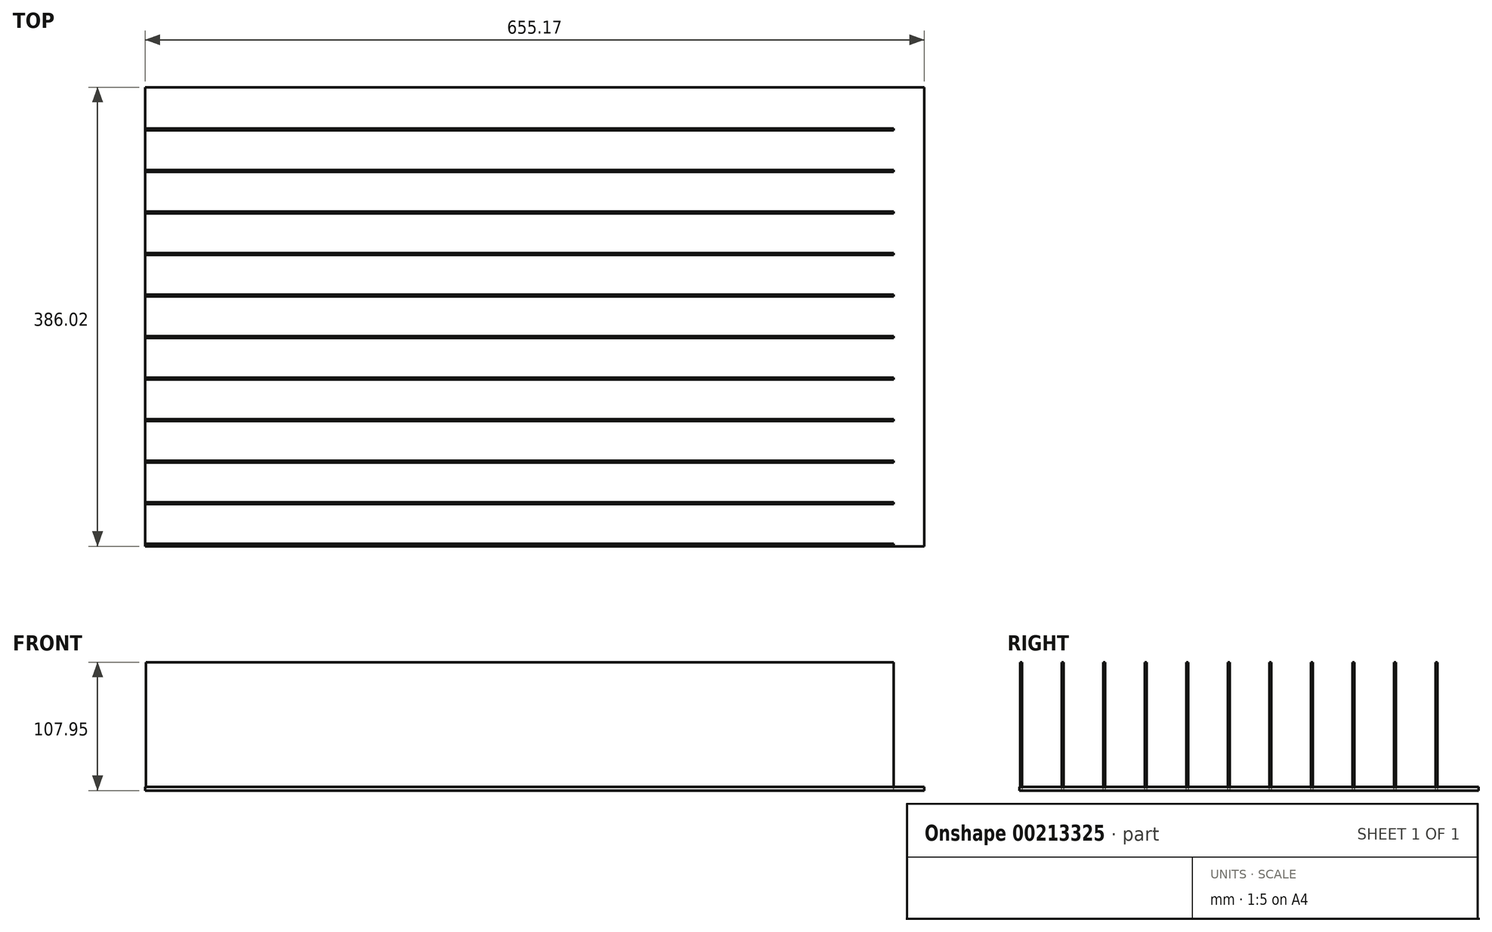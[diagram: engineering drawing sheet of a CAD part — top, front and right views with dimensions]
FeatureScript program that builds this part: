
annotation { "Feature Type Name" : "Feature", "Feature Type Description" : "" }
export const myFeature = defineFeature(function(context is Context, id is Id, definition is map)
    precondition{}
    {
        {
            var Q0;
            Q0=qCreatedBy(makeId("Right.planeOp"),FACE);
            var sketch = newSketch(context, id + "F0", { "sketchPlane" : qUnion([Q0])});
            skLineSegment(sketch, "E0", {"start": v(-1.59, 0) * mm, "end": v(-1.59, 107.95) * mm});
            skLineSegment(sketch, "E1", {"start": v(-1.59, 107.95) * mm, "end": v(0, 107.95) * mm});
            skLineSegment(sketch, "E2", {"start": v(0, 107.95) * mm, "end": v(0, 0) * mm});
            skLineSegment(sketch, "E3", {"start": v(0, 0) * mm, "end": v(-1.59, 0) * mm});
            skLineSegment(sketch, "E4.1.0.0", {"start": v(34.93, 107.95) * mm, "end": v(34.93, 0) * mm});
            skLineSegment(sketch, "E4.1.0.1", {"start": v(33.34, 0) * mm, "end": v(33.34, 107.95) * mm});
            skLineSegment(sketch, "E4.1.0.2", {"start": v(33.34, 107.95) * mm, "end": v(34.93, 107.95) * mm});
            skLineSegment(sketch, "E4.1.0.3", {"start": v(34.93, 0) * mm, "end": v(33.34, 0) * mm});
            skLineSegment(sketch, "E4.2.0.0", {"start": v(69.85, 107.95) * mm, "end": v(69.85, 0) * mm});
            skLineSegment(sketch, "E4.2.0.1", {"start": v(68.26, 0) * mm, "end": v(68.26, 107.95) * mm});
            skLineSegment(sketch, "E4.2.0.2", {"start": v(68.26, 107.95) * mm, "end": v(69.85, 107.95) * mm});
            skLineSegment(sketch, "E4.2.0.3", {"start": v(69.85, 0) * mm, "end": v(68.26, 0) * mm});
            skLineSegment(sketch, "E4.3.0.0", {"start": v(104.78, 107.95) * mm, "end": v(104.78, 0) * mm});
            skLineSegment(sketch, "E4.3.0.1", {"start": v(103.19, 0) * mm, "end": v(103.19, 107.95) * mm});
            skLineSegment(sketch, "E4.3.0.2", {"start": v(103.19, 107.95) * mm, "end": v(104.78, 107.95) * mm});
            skLineSegment(sketch, "E4.3.0.3", {"start": v(104.78, 0) * mm, "end": v(103.19, 0) * mm});
            skLineSegment(sketch, "E4.4.0.0", {"start": v(139.7, 107.95) * mm, "end": v(139.7, 0) * mm});
            skLineSegment(sketch, "E4.4.0.1", {"start": v(138.11, 0) * mm, "end": v(138.11, 107.95) * mm});
            skLineSegment(sketch, "E4.4.0.2", {"start": v(138.11, 107.95) * mm, "end": v(139.7, 107.95) * mm});
            skLineSegment(sketch, "E4.4.0.3", {"start": v(139.7, 0) * mm, "end": v(138.11, 0) * mm});
            skLineSegment(sketch, "E4.5.0.0", {"start": v(174.63, 107.95) * mm, "end": v(174.63, 0) * mm});
            skLineSegment(sketch, "E4.5.0.1", {"start": v(173.04, 0) * mm, "end": v(173.04, 107.95) * mm});
            skLineSegment(sketch, "E4.5.0.2", {"start": v(173.04, 107.95) * mm, "end": v(174.62, 107.95) * mm});
            skLineSegment(sketch, "E4.5.0.3", {"start": v(174.62, 0) * mm, "end": v(173.04, 0) * mm});
            skLineSegment(sketch, "E4.6.0.0", {"start": v(209.55, 107.95) * mm, "end": v(209.55, 0) * mm});
            skLineSegment(sketch, "E4.6.0.1", {"start": v(207.96, 0) * mm, "end": v(207.96, 107.95) * mm});
            skLineSegment(sketch, "E4.6.0.2", {"start": v(207.96, 107.95) * mm, "end": v(209.55, 107.95) * mm});
            skLineSegment(sketch, "E4.6.0.3", {"start": v(209.55, 0) * mm, "end": v(207.96, 0) * mm});
            skLineSegment(sketch, "E4.7.0.0", {"start": v(244.48, 107.95) * mm, "end": v(244.48, 0) * mm});
            skLineSegment(sketch, "E4.7.0.1", {"start": v(242.89, 0) * mm, "end": v(242.89, 107.95) * mm});
            skLineSegment(sketch, "E4.7.0.2", {"start": v(242.89, 107.95) * mm, "end": v(244.48, 107.95) * mm});
            skLineSegment(sketch, "E4.7.0.3", {"start": v(244.48, 0) * mm, "end": v(242.89, 0) * mm});
            skLineSegment(sketch, "E4.8.0.0", {"start": v(279.4, 107.95) * mm, "end": v(279.4, 0) * mm});
            skLineSegment(sketch, "E4.8.0.1", {"start": v(277.81, 0) * mm, "end": v(277.81, 107.95) * mm});
            skLineSegment(sketch, "E4.8.0.2", {"start": v(277.81, 107.95) * mm, "end": v(279.4, 107.95) * mm});
            skLineSegment(sketch, "E4.8.0.3", {"start": v(279.4, 0) * mm, "end": v(277.81, 0) * mm});
            skLineSegment(sketch, "E4.9.0.0", {"start": v(314.33, 107.95) * mm, "end": v(314.33, 0) * mm});
            skLineSegment(sketch, "E4.9.0.1", {"start": v(312.74, 0) * mm, "end": v(312.74, 107.95) * mm});
            skLineSegment(sketch, "E4.9.0.2", {"start": v(312.74, 107.95) * mm, "end": v(314.33, 107.95) * mm});
            skLineSegment(sketch, "E4.9.0.3", {"start": v(314.33, 0) * mm, "end": v(312.74, 0) * mm});
            skLineSegment(sketch, "E4.10.0.0", {"start": v(349.25, 107.95) * mm, "end": v(349.25, 0) * mm});
            skLineSegment(sketch, "E4.10.0.1", {"start": v(347.66, 0) * mm, "end": v(347.66, 107.95) * mm});
            skLineSegment(sketch, "E4.10.0.2", {"start": v(347.66, 107.95) * mm, "end": v(349.25, 107.95) * mm});
            skLineSegment(sketch, "E4.10.0.3", {"start": v(349.25, 0) * mm, "end": v(347.66, 0) * mm});
            skLineSegment(sketch, "E4.direction1", {"start": v(0, 0) * mm, "end": v(34.93, 0) * mm, "construction": true});
            skSolve(sketch);
        }
        {
            var Q0;
            Q0=makeQuery(id+"F0.imprint","IMPRINT",FACE,{"disambiguationData":[TD([[makeQuery(id+"F0.imprint","IMPRINT",EDGE,{"derivedFrom":sQuery(id+"F0.wireOp",EDGE,"E4.10.0.0")}),-1.0]])]});
            var Q1;
            Q1=makeQuery(id+"F0.imprint","IMPRINT",FACE,{"disambiguationData":[TD([[makeQuery(id+"F0.imprint","IMPRINT",EDGE,{"derivedFrom":sQuery(id+"F0.wireOp",EDGE,"E4.9.0.0")}),-1.0]])]});
            var Q2;
            Q2=makeQuery(id+"F0.imprint","IMPRINT",FACE,{"disambiguationData":[TD([[makeQuery(id+"F0.imprint","IMPRINT",EDGE,{"derivedFrom":sQuery(id+"F0.wireOp",EDGE,"E4.8.0.0")}),-1.0]])]});
            var Q3;
            Q3=makeQuery(id+"F0.imprint","IMPRINT",FACE,{"disambiguationData":[TD([[makeQuery(id+"F0.imprint","IMPRINT",EDGE,{"derivedFrom":sQuery(id+"F0.wireOp",EDGE,"E4.7.0.0")}),-1.0]])]});
            var Q4;
            Q4=makeQuery(id+"F0.imprint","IMPRINT",FACE,{"disambiguationData":[TD([[makeQuery(id+"F0.imprint","IMPRINT",EDGE,{"derivedFrom":sQuery(id+"F0.wireOp",EDGE,"E4.6.0.0")}),-1.0]])]});
            var Q5;
            Q5=makeQuery(id+"F0.imprint","IMPRINT",FACE,{"disambiguationData":[TD([[makeQuery(id+"F0.imprint","IMPRINT",EDGE,{"derivedFrom":sQuery(id+"F0.wireOp",EDGE,"E4.5.0.0")}),-1.0]])]});
            var Q6;
            Q6=makeQuery(id+"F0.imprint","IMPRINT",FACE,{"disambiguationData":[TD([[makeQuery(id+"F0.imprint","IMPRINT",EDGE,{"derivedFrom":sQuery(id+"F0.wireOp",EDGE,"E4.4.0.0")}),-1.0]])]});
            var Q7;
            Q7=makeQuery(id+"F0.imprint","IMPRINT",FACE,{"disambiguationData":[TD([[makeQuery(id+"F0.imprint","IMPRINT",EDGE,{"derivedFrom":sQuery(id+"F0.wireOp",EDGE,"E4.3.0.0")}),-1.0]])]});
            var Q8;
            Q8=makeQuery(id+"F0.imprint","IMPRINT",FACE,{"disambiguationData":[TD([[makeQuery(id+"F0.imprint","IMPRINT",EDGE,{"derivedFrom":sQuery(id+"F0.wireOp",EDGE,"E4.2.0.0")}),-1.0]])]});
            var Q9;
            Q9=makeQuery(id+"F0.imprint","IMPRINT",FACE,{"disambiguationData":[TD([[makeQuery(id+"F0.imprint","IMPRINT",EDGE,{"derivedFrom":sQuery(id+"F0.wireOp",EDGE,"E4.1.0.0")}),-1.0]])]});
            var Q10;
            Q10=makeQuery(id+"F0.imprint","IMPRINT",FACE,{"disambiguationData":[TD([[makeQuery(id+"F0.imprint","IMPRINT",EDGE,{"derivedFrom":sQuery(id+"F0.wireOp",EDGE,"E0")}),-1.0]])]});
            extrude(context, id + "F1", {"entities" : qUnion([Q0, Q1, Q2, Q3, Q4, Q5, Q6, Q7, Q8, Q9, Q10]), "endBound" : BoundingType.SYMMETRIC, "depth" : 628.65 * mm});
        }
        {
            var Q0;
            Q0=qCreatedBy(makeId("Top.planeOp"),FACE);
            var sketch = newSketch(context, id + "F2", { "sketchPlane" : qUnion([Q0])});
            skLineSegment(sketch, "E5.bottom", {"start": v(-315.06, -2.15) * mm, "end": v(340.1, -2.15) * mm});
            skLineSegment(sketch, "E5.top", {"start": v(-315.06, 383.87) * mm, "end": v(340.1, 383.87) * mm});
            skLineSegment(sketch, "E5.left", {"start": v(-315.06, -2.15) * mm, "end": v(-315.06, 383.87) * mm});
            skLineSegment(sketch, "E5.right", {"start": v(340.1, -2.15) * mm, "end": v(340.1, 383.87) * mm});
            skSolve(sketch);
        }
        {
            var Q0;
            Q0 = qSketchRegion(id + "F2", true);
            extrude(context, id + "F3", {"entities" : qUnion([Q0]), "depth" : 3.17 * mm});
        }
    });
